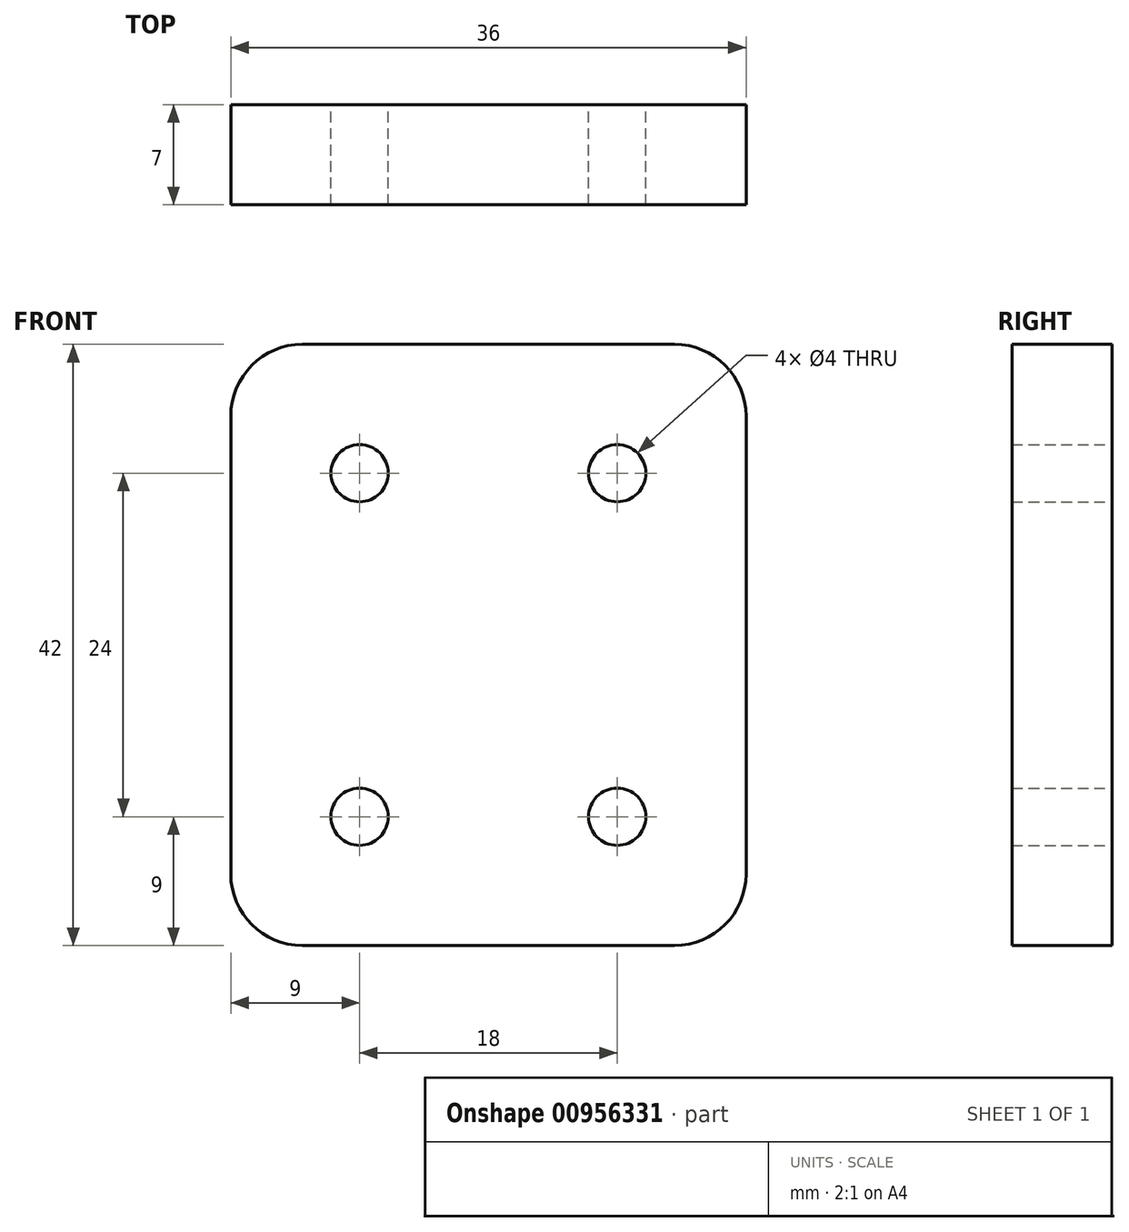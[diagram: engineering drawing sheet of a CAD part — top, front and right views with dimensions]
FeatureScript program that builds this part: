
annotation { "Feature Type Name" : "Feature", "Feature Type Description" : "" }
export const myFeature = defineFeature(function(context is Context, id is Id, definition is map)
    precondition{}
    {
        {
            var Q0;
            Q0=qCreatedBy(makeId("Front.planeOp"),FACE);
            var sketch = newSketch(context, id + "F0", { "sketchPlane" : qUnion([Q0])});
            skLineSegment(sketch, "E0.bottom", {"start": v(0, 0) * mm, "end": v(36, 0) * mm});
            skLineSegment(sketch, "E0.top", {"start": v(0, 42) * mm, "end": v(36, 42) * mm});
            skLineSegment(sketch, "E0.left", {"start": v(0, 0) * mm, "end": v(0, 42) * mm});
            skLineSegment(sketch, "E0.right", {"start": v(36, 0) * mm, "end": v(36, 42) * mm});
            skLineSegment(sketch, "E1", {"start": v(18, 42) * mm, "end": v(18, 0) * mm, "construction": true});
            skCircle(sketch, "E2", {"center": v(9, 33) * mm, "radius": 2 * mm});
            skCircle(sketch, "E3", {"center": v(9, 9) * mm, "radius": 2 * mm});
            skLineSegment(sketch, "E4", {"start": v(9, 33) * mm, "end": v(9, 9) * mm, "construction": true});
            skLineSegment(sketch, "E5", {"start": v(9, 9) * mm, "end": v(18, 9) * mm, "construction": true});
            skLineSegment(sketch, "E6", {"start": v(9, 9) * mm, "end": v(9, 0) * mm, "construction": true});
            skLineSegment(sketch, "E7", {"start": v(9, 9) * mm, "end": v(0, 9) * mm, "construction": true});
            skLineSegment(sketch, "E8", {"start": v(9, 33) * mm, "end": v(9, 42) * mm, "construction": true});
            skCircle(sketch, "E9.MirrorC", {"center": v(27, 33) * mm, "radius": 2 * mm});
            skCircle(sketch, "E10.MirrorC", {"center": v(27, 9) * mm, "radius": 2 * mm});
            skSolve(sketch);
        }
        {
            var Q0;
            Q0=makeQuery(id+"F0.imprint","IMPRINT",FACE,{"disambiguationData":[TD([[makeQuery(id+"F0.imprint","IMPRINT",EDGE,{"derivedFrom":sQuery(id+"F0.wireOp",EDGE,"E0.bottom")}),1.0]])]});
            extrude(context, id + "F1", {"entities" : qUnion([Q0]), "depth" : 7 * mm, "offsetDistance" : 25 * mm});
        }
        {
            var Q0;
            Q0=makeQuery(id+"F1.opExtrude","SWEPT_EDGE",EDGE,{"disambiguationData":[OSD([sQuery(id+"F0.wireOp",EDGE,"E0.top"),sQuery(id+"F0.wireOp",EDGE,"E0.left")])]});
            var Q1;
            Q1=makeQuery(id+"F1.opExtrude","SWEPT_EDGE",EDGE,{"disambiguationData":[OSD([sQuery(id+"F0.wireOp",EDGE,"E0.bottom"),sQuery(id+"F0.wireOp",EDGE,"E0.left")])]});
            var Q2;
            Q2=makeQuery(id+"F1.opExtrude","SWEPT_EDGE",EDGE,{"disambiguationData":[OSD([sQuery(id+"F0.wireOp",EDGE,"E0.bottom"),sQuery(id+"F0.wireOp",EDGE,"E0.right")])]});
            var Q3;
            Q3=makeQuery(id+"F1.opExtrude","SWEPT_EDGE",EDGE,{"disambiguationData":[OSD([sQuery(id+"F0.wireOp",EDGE,"E0.top"),sQuery(id+"F0.wireOp",EDGE,"E0.right")])]});
            fillet(context, id + "F2", {"entities" : qUnion([Q0, Q1, Q2, Q3]), "radius" : 5 * mm, "tangentPropagation" : true, "allowEdgeOverflow" : false});
        }
    });
